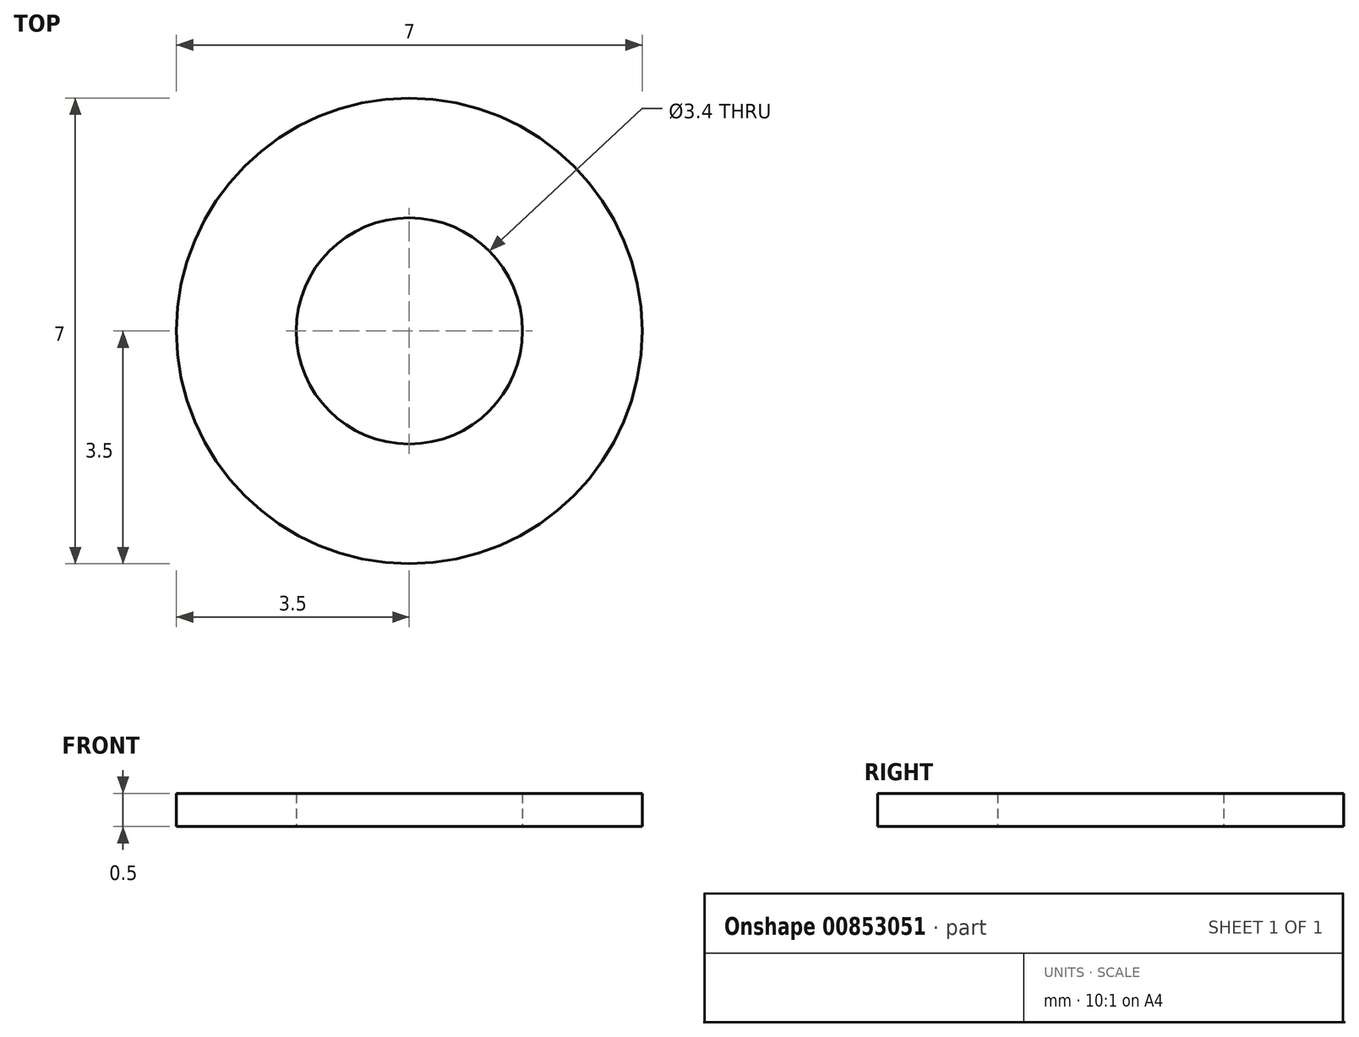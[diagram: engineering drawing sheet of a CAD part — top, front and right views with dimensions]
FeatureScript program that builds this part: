
annotation { "Feature Type Name" : "Feature", "Feature Type Description" : "" }
export const myFeature = defineFeature(function(context is Context, id is Id, definition is map)
    precondition{}
    {
        {
            var Q0;
            Q0=qCreatedBy(makeId("Top.planeOp"),FACE);
            var sketch = newSketch(context, id + "F0", { "sketchPlane" : qUnion([Q0])});
            skCircle(sketch, "E0", {"center": v(0, 0) * mm, "radius": 3.5 * mm});
            skCircle(sketch, "E1", {"center": v(0, 0) * mm, "radius": 1.7 * mm});
            skSolve(sketch);
        }
        {
            var Q0;
            Q0 = qSketchRegion(id + "F0", true);
            extrude(context, id + "F1", {"entities" : qUnion([Q0]), "depth" : 0.5 * mm, "offsetDistance" : 25 * mm});
        }
    });
